# Revit family: NBS_DudleyIndustries_SoapDpnsrs_PlatinumRange_FoamSoapDispenser
name_source: partatom
category: Specialty Equipment
revit_build: Autodesk Revit 2016 (Build: 20150220_1215(x64)
units: mm (PartAtom-declared; Revit-internal decimal feet)

## family parameters
Cut with Voids When Loaded = No
Host = Face
OmniClass Number = 23.40.20.21.34
OmniClass Title = Soap Holders, Dispensers
Part Type = Normal
Room Calculation Point = No
Round Connector Dimension = Use Diameter
Shared = No

## types (1)
- PlatinumRangeFoamSoapDispenser
    AssetType = Fixed
    BIMObjectName = NBS_DudleyIndustries_SoapDispensers_Platinumrange_FoamSoapDispenser
    Category = Pr_40_70_22_81:Soap dispensers
    Color = Stainless Steel
    Default Elevation = 1200 mm
    Description = Foam Soap Dispenser (Refill)
    DispenserCasingMaterial = NBS_Concept
    DispenserLockMaterial = NBS_Concept
    DurationUnit = year
    ExpectedLife = 5
    Finish = Brushed/Lacquered (50015CB)
    Form = Wall mounted
    IfcExportAs = IfcFurnitureType
    IfcExportType = NOTDEFINED
    MainColor = Stainless Steel
    ManufacturerName = Dudley Industries
    ManufacturerURL = www.dudleyindustries.com/
    Material = Stainless Steel
    MaterialsBody = Stainless Steel
    ModelNumber = 50015
    ModelReference = Platinum range: Foam Soap Dispenser
    NBSCertification = www.nationalbimlibrary.com/cert/bgu1zt5g
    NBSDescription = Soap dispensers
    NBSReference = 45-35-72/358
    Name = SoapDispensers_PlatinumRange_FoamSoapDispenser_DudleyIndustries
    NominalDepth = 102 mm
    NominalHeight = 252 mm  [stored 0.826772 ft]
    NominalLength = 120 mm  [stored 0.393701 ft]
    NominalWidth = 120 mm  [stored 0.393701 ft]
    Operation = Manual push operation
    ProductInformation = www.dudleyindustries.com/wp-content/uploads/2016/11/Platinum_1-Lt-Foam_Soap_Dispenser_Refill.pdf
    Size = 120 x 252 x 102 mm
    Style = Soap dispenser
    Uniclass2015Code = Pr_40_70_22_81
    Uniclass2015Title = Soap dispensers
    Uniclass2015Version = Products v1.7
    Version = 2
    WarrantyDescription = 1 year warranty
    WarrantyDurationParts = 1
    WarrantyDurationUnit = year

note: [stored X ft] marks values corroborated as IEEE doubles in the binary element streams (Revit-internal decimal feet)

## geometry (parser evidence)
native form markers: Sweep x2
no freeform markers — native parametric forms only
